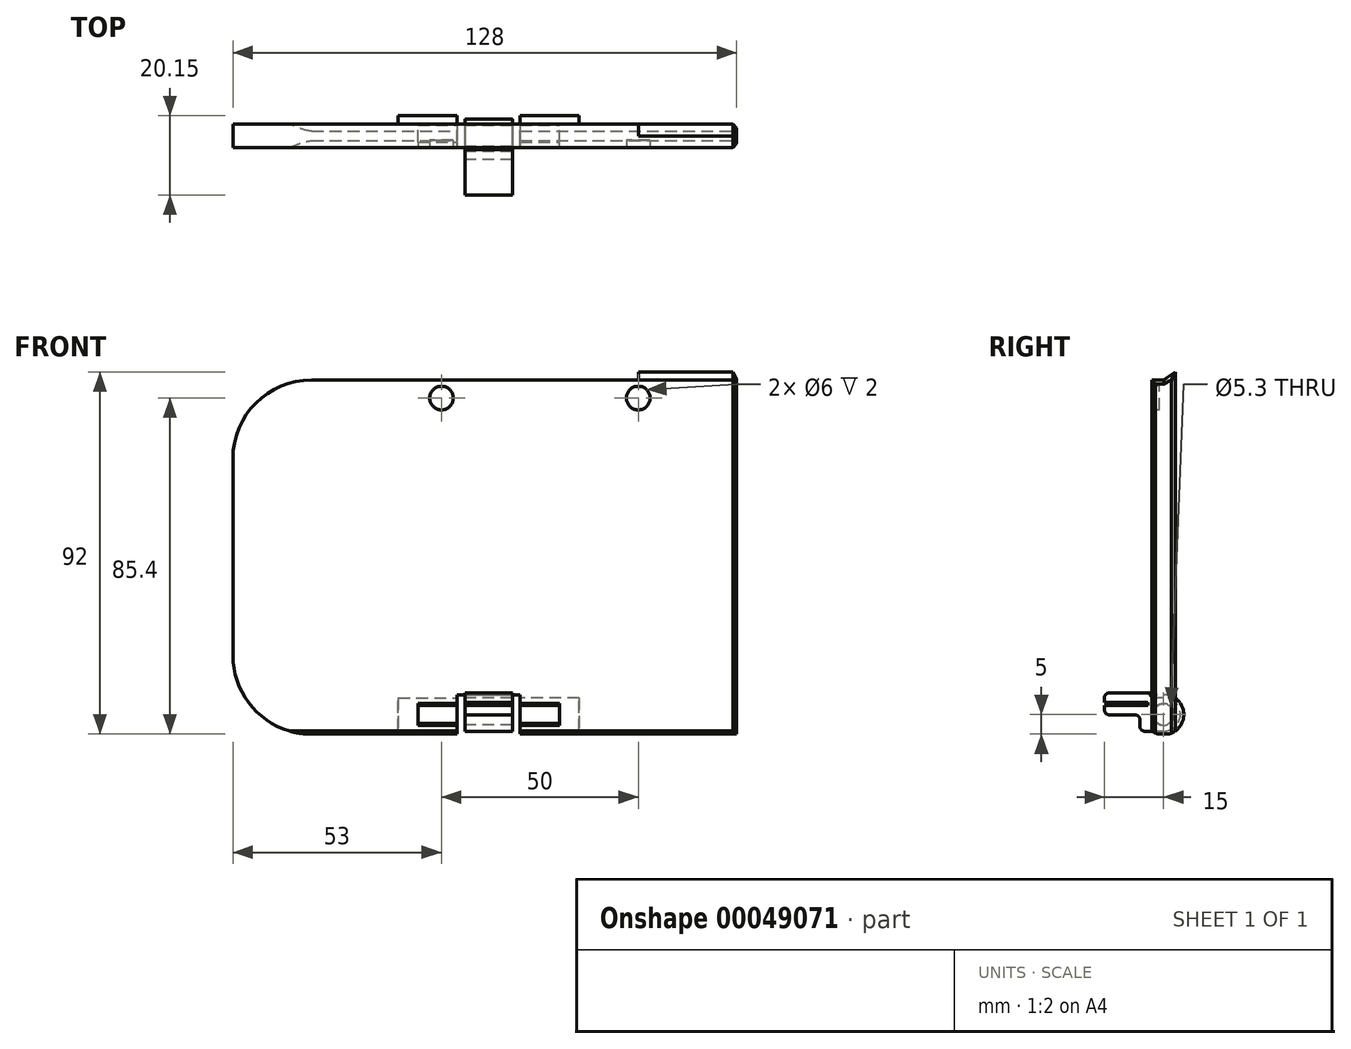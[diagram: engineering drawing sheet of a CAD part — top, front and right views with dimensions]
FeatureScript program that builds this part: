
annotation { "Feature Type Name" : "Feature", "Feature Type Description" : "" }
export const myFeature = defineFeature(function(context is Context, id is Id, definition is map)
    precondition{}
    {
        {
            var Q0;
            Q0=qCreatedBy(makeId("Front.planeOp"),FACE);
            var sketch = newSketch(context, id + "F0", { "sketchPlane" : qUnion([Q0])});
            skLineSegment(sketch, "E0.bottom", {"start": v(0, -45) * mm, "end": v(-108, -45) * mm});
            skLineSegment(sketch, "E0.top", {"start": v(0, 45) * mm, "end": v(-108, 45) * mm});
            skLineSegment(sketch, "E0.left", {"start": v(0, -45) * mm, "end": v(0, 45) * mm});
            skLineSegment(sketch, "E0.right", {"start": v(-128, -25) * mm, "end": v(-128, 25) * mm});
            skPoint(sketch, "E1.visualSharp", {"position": v(-128, 45) * mm});
            skArc(sketch, "E1.filletArc", {"start": v(-108, 45) * mm, "mid": v(-122.14, 39.14) * mm, "end": v(-128, 25) * mm});
            skPoint(sketch, "E2.visualSharp", {"position": v(-128, -45) * mm});
            skArc(sketch, "E2.filletArc", {"start": v(-128, -25) * mm, "mid": v(-122.14, -39.14) * mm, "end": v(-108, -45) * mm});
            skSolve(sketch);
        }
        {
            var Q0;
            Q0 = qSketchRegion(id + "F0", true);
            extrude(context, id + "F1", {"entities" : qUnion([Q0]), "depth" : 6 * mm, "offsetDistance" : 25 * mm});
        }
        {
            var Q0;
            Q0=makeQuery(id+"F1.opExtrude","CAP_FACE",FACE,{"disambiguationData":[OSD([sQuery(id+"F0.wireOp",EDGE,"E0.bottom"),sQuery(id+"F0.wireOp",EDGE,"E0.top"),sQuery(id+"F0.wireOp",EDGE,"E0.left"),sQuery(id+"F0.wireOp",EDGE,"E0.right"),sQuery(id+"F0.wireOp",EDGE,"E1.filletArc"),sQuery(id+"F0.wireOp",EDGE,"E2.filletArc")])],"isStart":false});
            var sketch = newSketch(context, id + "F2", { "sketchPlane" : qUnion([Q0])});
            skLineSegment(sketch, "E3.bottom", {"start": v(-71, -45) * mm, "end": v(-55, -45) * mm});
            skLineSegment(sketch, "E3.top", {"start": v(-71, -35) * mm, "end": v(-55, -35) * mm});
            skLineSegment(sketch, "E3.left", {"start": v(-71, -45) * mm, "end": v(-71, -35) * mm});
            skLineSegment(sketch, "E3.right", {"start": v(-55, -45) * mm, "end": v(-55, -35) * mm});
            skSolve(sketch);
        }
        {
            var Q0;
            Q0 = qSketchRegion(id + "F2", true);
            extrude(context, id + "F3", {"entities" : qUnion([Q0]), "operationType" : NewBodyOperationType.REMOVE, "endBound" : BoundingType.THROUGH_ALL, "oppositeDirection" : true, "depth" : 25 * mm, "offsetDistance" : 25 * mm});
        }
        {
            var Q0;
            Q0=makeQuery(id+"F3.boolean.opBoolean","COPY",FACE,{"derivedFrom":makeQuery(id+"F3.opExtrude","SWEPT_FACE",FACE,{"disambiguationData":[OSD([sQuery(id+"F2.wireOp",EDGE,"E3.left")])]})});
            var Q1;
            Q1=makeQuery(id+"F3.boolean.opBoolean","COPY",FACE,{"derivedFrom":makeQuery(id+"F3.opExtrude","SWEPT_FACE",FACE,{"disambiguationData":[OSD([sQuery(id+"F2.wireOp",EDGE,"E3.right")])]})});
            cPlane(context, id + "F4", {"entities" : qUnion([Q0, Q1]), "cplaneType" : CPlaneType.MID_PLANE, "offset" : 25 * mm, "width" : 150 * mm, "height" : 150 * mm});
        }
        {
            var Q0;
            Q0=qCreatedBy(id+"F4.planeOp",FACE);
            var sketch = newSketch(context, id + "F5", { "sketchPlane" : qUnion([Q0])});
            skLineSegment(sketch, "E4.0.0", {"start": v(0, -45) * mm, "end": v(0, -35) * mm, "construction": true});
            skLineSegment(sketch, "E4.0.1", {"start": v(0, -35) * mm, "end": v(-6, -35) * mm, "construction": true});
            skLineSegment(sketch, "E4.0.2", {"start": v(-6, -35) * mm, "end": v(-6, -45) * mm, "construction": true});
            skLineSegment(sketch, "E4.0.3", {"start": v(-6, -45) * mm, "end": v(0, -45) * mm, "construction": true});
            skArc(sketch, "E5", {"start": v(-4.58, -42.25) * mm, "mid": v(-0.25, -40) * mm, "end": v(-4.58, -37.75) * mm});
            skPoint(sketch, "E5.centerSnap0", {"position": v(-3, -45) * mm});
            skPoint(sketch, "E5.centerSnap1", {"position": v(0, -40) * mm});
            skLineSegment(sketch, "E6", {"start": v(-4.58, -42.25) * mm, "end": v(-6, -42.75) * mm});
            skLineSegment(sketch, "E7", {"start": v(-6, -42.75) * mm, "end": v(-6, -37.25) * mm});
            skLineSegment(sketch, "E8", {"start": v(-6, -37.25) * mm, "end": v(-4.58, -37.75) * mm});
            skLineSegment(sketch, "E9", {"start": v(-4.58, -42.25) * mm, "end": v(-4.58, -37.75) * mm, "construction": true});
            skLineSegment(sketch, "E10", {"start": v(-4.58, -40) * mm, "end": v(-6, -40) * mm, "construction": true});
            skSolve(sketch);
        }
        {
            var Q0;
            Q0=makeQuery(id+"F5.imprint","IMPRINT",FACE,{"disambiguationData":[TD([[makeQuery(id+"F5.imprint","IMPRINT",EDGE,{"derivedFrom":sQuery(id+"F5.wireOp",EDGE,"E5")}),1.0]])]});
            extrude(context, id + "F6", {"entities" : qUnion([Q0]), "operationType" : NewBodyOperationType.REMOVE, "oppositeDirection" : true, "depth" : 18 * mm, "offsetDistance" : 25 * mm, "hasSecondDirection" : true, "secondDirectionOppositeDirection" : false, "secondDirectionDepth" : 18 * mm});
        }
        {
            var Q0;
            Q0=makeQuery(id+"F3.boolean.opBoolean","COPY",FACE,{"derivedFrom":makeQuery(id+"F3.opExtrude","SWEPT_FACE",FACE,{"disambiguationData":[OSD([sQuery(id+"F2.wireOp",EDGE,"E3.right")])]})});
            var sketch = newSketch(context, id + "F7", { "sketchPlane" : qUnion([Q0])});
            skArc(sketch, "E11", {"start": v(6, -35.81) * mm, "mid": v(-2.15, -40) * mm, "end": v(6, -44.19) * mm});
            skLineSegment(sketch, "E12", {"start": v(6, -42.75) * mm, "end": v(6, -44.19) * mm});
            skLineSegment(sketch, "E13", {"start": v(6, -37.25) * mm, "end": v(6, -35.81) * mm});
            skSolve(sketch);
        }
        {
            var Q0;
            {var subQ0=sQuery(id+"F7.wireOp",EDGE,"E11");var subQ1=makeQuery(id+"F3.boolean.opBoolean","INTERSECT",EDGE,{"derivedFrom":[makeQuery(id+"F1.opExtrude","CAP_FACE",FACE,{"disambiguationData":[OSD([sQuery(id+"F0.wireOp",EDGE,"E0.bottom"),sQuery(id+"F0.wireOp",EDGE,"E0.top"),sQuery(id+"F0.wireOp",EDGE,"E0.left"),sQuery(id+"F0.wireOp",EDGE,"E0.right"),sQuery(id+"F0.wireOp",EDGE,"E1.filletArc"),sQuery(id+"F0.wireOp",EDGE,"E2.filletArc")])],"isStart":true}),makeQuery(id+"F3.opExtrude","SWEPT_FACE",FACE,{"disambiguationData":[OSD([sQuery(id+"F2.wireOp",EDGE,"E3.right")])]})]});var subQ2=makeQuery(id+"F7.imprint","INTERSECT",VERTEX,{"disambiguationData":[OD(0.0)],"derivedFrom":[subQ1,subQ0]});Q0=makeQuery(id+"F7.imprint","IMPRINT",FACE,{"disambiguationData":[TD([[makeQuery(id+"F7.imprint","IMPRINT",EDGE,{"disambiguationData":[TD([[subQ2,-1.0]])],"derivedFrom":subQ0}),1.0]])]});}
            extrude(context, id + "F8", {"entities" : qUnion([Q0]), "oppositeDirection" : true, "depth" : 15 * mm, "offsetDistance" : 25 * mm});
        }
        {
            var Q0;
            Q0=makeQuery(id+"F8.opExtrude","SWEPT_BODY",BODY,{"disambiguationData":[OSD([sQuery(id+"F0.wireOp",EDGE,"E0.bottom"),sQuery(id+"F0.wireOp",EDGE,"E0.top"),sQuery(id+"F0.wireOp",EDGE,"E0.left"),sQuery(id+"F0.wireOp",EDGE,"E0.right"),sQuery(id+"F0.wireOp",EDGE,"E1.filletArc"),sQuery(id+"F0.wireOp",EDGE,"E2.filletArc"),sQuery(id+"F2.wireOp",EDGE,"E3.bottom"),sQuery(id+"F2.wireOp",EDGE,"E3.top"),sQuery(id+"F2.wireOp",EDGE,"E3.right"),sQuery(id+"F7.wireOp",EDGE,"E11"),sQuery(id+"F7.wireOp",EDGE,"E12"),sQuery(id+"F7.wireOp",EDGE,"E13")])]});
            var Q1;
            Q1=qCreatedBy(id+"F4.planeOp",FACE);
            mirror(context, id + "F9", {"operationType" : NewBodyOperationType.ADD, "entities" : qUnion([Q0]), "mirrorPlane" : qUnion([Q1])});
        }
        {
            var Q0;
            Q0=makeQuery(id+"F1.opExtrude","SWEPT_FACE",FACE,{"disambiguationData":[OSD([sQuery(id+"F0.wireOp",EDGE,"E0.left")])]});
            var sketch = newSketch(context, id + "F10", { "sketchPlane" : qUnion([Q0])});
            skLineSegment(sketch, "E14", {"start": v(0, 45) * mm, "end": v(0, 47) * mm});
            skLineSegment(sketch, "E15", {"start": v(0, 47) * mm, "end": v(-3, 45) * mm});
            skLineSegment(sketch, "E16", {"start": v(-3, 45) * mm, "end": v(0, 45) * mm});
            skSolve(sketch);
        }
        {
            var Q0;
            Q0 = qSketchRegion(id + "F10", true);
            extrude(context, id + "F11", {"entities" : qUnion([Q0]), "operationType" : NewBodyOperationType.ADD, "oppositeDirection" : true, "depth" : 25 * mm, "offsetDistance" : 25 * mm});
        }
        {
            var Q0;
            Q0=makeQuery(id+"F11.boolean.opBoolean","MERGE",FACE,{"derivedFrom":[makeQuery(id+"F1.opExtrude","SWEPT_FACE",FACE,{"disambiguationData":[OSD([sQuery(id+"F0.wireOp",EDGE,"E0.left")])]}),makeQuery(id+"F11.opExtrude","CAP_FACE",FACE,{"disambiguationData":[OSD([sQuery(id+"F10.wireOp",EDGE,"E14"),sQuery(id+"F10.wireOp",EDGE,"E15"),sQuery(id+"F10.wireOp",EDGE,"E16")])],"isStart":true})]});
            var sketch = newSketch(context, id + "F12", { "sketchPlane" : qUnion([Q0])});
            skArc(sketch, "E17.0", {"start": v(0, -35.81) * mm, "mid": v(2.15, -40) * mm, "end": v(0, -44.19) * mm, "construction": true});
            skArc(sketch, "E18", {"start": v(-6, -44.19) * mm, "mid": v(1.19, -43) * mm, "end": v(0, -35.81) * mm});
            skLineSegment(sketch, "E19", {"start": v(-6, -44.19) * mm, "end": v(-6, -45) * mm});
            skLineSegment(sketch, "E20", {"start": v(-6, -45) * mm, "end": v(0, -45) * mm});
            skLineSegment(sketch, "E21", {"start": v(0, -45) * mm, "end": v(0, -44.19) * mm});
            skSolve(sketch);
        }
        {
            var Q0;
            {var subQ0=sQuery(id+"F12.wireOp",EDGE,"E19");Q0=makeQuery(id+"F12.imprint","IMPRINT",FACE,{"disambiguationData":[TD([[makeQuery(id+"F12.imprint","IMPRINT",EDGE,{"derivedFrom":subQ0}),-1.0]])]});}
            var Q1;
            {var subQ0=sQuery(id+"F12.wireOp",EDGE,"E21");Q1=makeQuery(id+"F12.imprint","IMPRINT",FACE,{"disambiguationData":[TD([[makeQuery(id+"F12.imprint","IMPRINT",EDGE,{"derivedFrom":subQ0}),1.0]])]});}
            extrude(context, id + "F13", {"entities" : qUnion([Q0, Q1]), "operationType" : NewBodyOperationType.REMOVE, "endBound" : BoundingType.THROUGH_ALL, "oppositeDirection" : true, "depth" : 25 * mm, "offsetDistance" : 25 * mm});
        }
        {
            var Q0;
            Q0=makeQuery(id+"F1.opExtrude","CAP_FACE",FACE,{"disambiguationData":[OSD([sQuery(id+"F0.wireOp",EDGE,"E0.bottom"),sQuery(id+"F0.wireOp",EDGE,"E0.top"),sQuery(id+"F0.wireOp",EDGE,"E0.left"),sQuery(id+"F0.wireOp",EDGE,"E0.right"),sQuery(id+"F0.wireOp",EDGE,"E1.filletArc"),sQuery(id+"F0.wireOp",EDGE,"E2.filletArc")])],"isStart":false});
            var sketch = newSketch(context, id + "F14", { "sketchPlane" : qUnion([Q0])});
            skCircle(sketch, "E22", {"center": v(-25, 40.4) * mm, "radius": 3 * mm});
            skCircle(sketch, "E23", {"center": v(-75, 40.4) * mm, "radius": 3 * mm});
            skSolve(sketch);
        }
        {
            var Q0;
            Q0 = qSketchRegion(id + "F14", true);
            var Q1;
            Q1=sQuery(id+"F14.wireOp",EDGE,"E22");
            extrude(context, id + "F15", {"entities" : qUnion([Q0]), "operationType" : NewBodyOperationType.REMOVE, "surfaceEntities" : qUnion([Q1]), "oppositeDirection" : true, "depth" : 2 * mm, "offsetDistance" : 25 * mm});
        }
        {
            var Q0;
            Q0=makeQuery(id+"F1.opExtrude","CAP_EDGE",EDGE,{"disambiguationData":[OSD([sQuery(id+"F0.wireOp",EDGE,"E0.left")])],"isStart":false});
            var Q1;
            Q1=makeQuery(id+"F11.boolean.opBoolean","MERGE",EDGE,{"derivedFrom":[makeQuery(id+"F1.opExtrude","CAP_EDGE",EDGE,{"disambiguationData":[OSD([sQuery(id+"F0.wireOp",EDGE,"E0.left")])],"isStart":true}),makeQuery(id+"F11.opExtrude","CAP_EDGE",EDGE,{"disambiguationData":[OSD([sQuery(id+"F10.wireOp",EDGE,"E14")])],"isStart":true})]});
            var Q2;
            Q2=makeQuery(id+"F1.opExtrude","SWEPT_EDGE",EDGE,{"disambiguationData":[OSD([sQuery(id+"F0.wireOp",EDGE,"E0.top"),sQuery(id+"F0.wireOp",EDGE,"E0.left")])]});
            var Q3;
            Q3=makeQuery(id+"F11.opExtrude","CAP_EDGE",EDGE,{"disambiguationData":[OSD([sQuery(id+"F10.wireOp",EDGE,"E15")])],"isStart":true});
            var Q4;
            Q4=makeQuery(id+"F13.boolean.opBoolean","COPY",EDGE,{"derivedFrom":makeQuery(id+"F13.opExtrude","CAP_EDGE",EDGE,{"disambiguationData":[OSD([sQuery(id+"F12.wireOp",EDGE,"E18")])],"isStart":true})});
            chamfer(context, id + "F16", {"entities" : qUnion([Q0, Q1, Q2, Q3, Q4]), "width" : 1 * mm, "tangentPropagation" : true});
        }
        {
            var Q0;
            Q0=qCreatedBy(id+"F4.planeOp",FACE);
            var sketch = newSketch(context, id + "F17", { "sketchPlane" : qUnion([Q0])});
            skArc(sketch, "E24.0.0", {"start": v(-4.23, -45) * mm, "mid": v(-5.16, -44.68) * mm, "end": v(-6, -44.19) * mm, "construction": true});
            skLineSegment(sketch, "E24.0.1", {"start": v(-6, -44.19) * mm, "end": v(-6, -42.75) * mm, "construction": true});
            skLineSegment(sketch, "E24.0.2", {"start": v(-6, -42.75) * mm, "end": v(-4.58, -42.25) * mm, "construction": true});
            skArc(sketch, "E24.0.3", {"start": v(-4.58, -42.25) * mm, "mid": v(-0.25, -40) * mm, "end": v(-4.58, -37.75) * mm, "construction": true});
            skLineSegment(sketch, "E24.0.4", {"start": v(-4.58, -37.75) * mm, "end": v(-6, -37.25) * mm, "construction": true});
            skLineSegment(sketch, "E24.0.5", {"start": v(-6, -37.25) * mm, "end": v(-6, -35) * mm, "construction": true});
            skLineSegment(sketch, "E24.0.6", {"start": v(-6, -35) * mm, "end": v(0, -35) * mm, "construction": true});
            skLineSegment(sketch, "E24.0.7", {"start": v(0, -35) * mm, "end": v(0, -35.81) * mm, "construction": true});
            skArc(sketch, "E24.0.8", {"start": v(0, -35.81) * mm, "mid": v(2.06, -40.97) * mm, "end": v(-1.77, -45) * mm, "construction": true});
            skLineSegment(sketch, "E24.0.9", {"start": v(-1.77, -45) * mm, "end": v(-4.23, -45) * mm, "construction": true});
            skArc(sketch, "E25", {"start": v(-3, -44.25) * mm, "mid": v(1.25, -40) * mm, "end": v(-3, -35.75) * mm});
            skCircle(sketch, "E26", {"center": v(-3, -40) * mm, "radius": 2.65 * mm});
            skLineSegment(sketch, "E27", {"start": v(-18, -35.7) * mm, "end": v(-18, -36.9) * mm});
            skLineSegment(sketch, "E28", {"start": v(-18, -36.9) * mm, "end": v(-7, -36.9) * mm});
            skLineSegment(sketch, "E29", {"start": v(-7, -36.9) * mm, "end": v(-7, -37.7) * mm});
            skLineSegment(sketch, "E30", {"start": v(-7, -37.7) * mm, "end": v(-18, -37.7) * mm});
            skLineSegment(sketch, "E31", {"start": v(-18, -37.7) * mm, "end": v(-18, -38.9) * mm});
            skLineSegment(sketch, "E32", {"start": v(-3, -35.75) * mm, "end": v(-5.3, -35.75) * mm});
            skLineSegment(sketch, "E33", {"start": v(-6.5, -34.55) * mm, "end": v(-6.5, -34.5) * mm});
            skLineSegment(sketch, "E34", {"start": v(-6.5, -34.5) * mm, "end": v(-16.8, -34.5) * mm});
            skPoint(sketch, "E35.visualSharp", {"position": v(-6, -35.75) * mm});
            skArc(sketch, "E35.filletArc", {"start": v(-6.5, -34.55) * mm, "mid": v(-6.15, -35.4) * mm, "end": v(-5.3, -35.75) * mm});
            skLineSegment(sketch, "E36", {"start": v(-3, -44.25) * mm, "end": v(-7.8, -44.25) * mm});
            skLineSegment(sketch, "E37", {"start": v(-9, -43.05) * mm, "end": v(-9, -41.3) * mm});
            skLineSegment(sketch, "E38", {"start": v(-10.2, -40.1) * mm, "end": v(-16.8, -40.1) * mm});
            skPoint(sketch, "E39.visualSharp", {"position": v(-9, -44.25) * mm});
            skArc(sketch, "E39.filletArc", {"start": v(-9, -43.05) * mm, "mid": v(-8.65, -43.9) * mm, "end": v(-7.8, -44.25) * mm});
            skPoint(sketch, "E40.visualSharp", {"position": v(-9, -40.1) * mm});
            skArc(sketch, "E40.filletArc", {"start": v(-9, -41.3) * mm, "mid": v(-9.35, -40.45) * mm, "end": v(-10.2, -40.1) * mm});
            skPoint(sketch, "E41.visualSharp", {"position": v(-18, -34.5) * mm});
            skArc(sketch, "E41.filletArc", {"start": v(-16.8, -34.5) * mm, "mid": v(-17.65, -34.85) * mm, "end": v(-18, -35.7) * mm});
            skPoint(sketch, "E42.visualSharp", {"position": v(-18, -40.1) * mm});
            skArc(sketch, "E42.filletArc", {"start": v(-18, -38.9) * mm, "mid": v(-17.65, -39.75) * mm, "end": v(-16.8, -40.1) * mm});
            skSolve(sketch);
        }
        {
            var Q0;
            Q0 = qSketchRegion(id + "F17", true);
            extrude(context, id + "F18", {"entities" : qUnion([Q0]), "depth" : 6 * mm, "offsetDistance" : 25 * mm, "hasSecondDirection" : true, "secondDirectionOppositeDirection" : true, "secondDirectionDepth" : 6 * mm});
        }
    });
